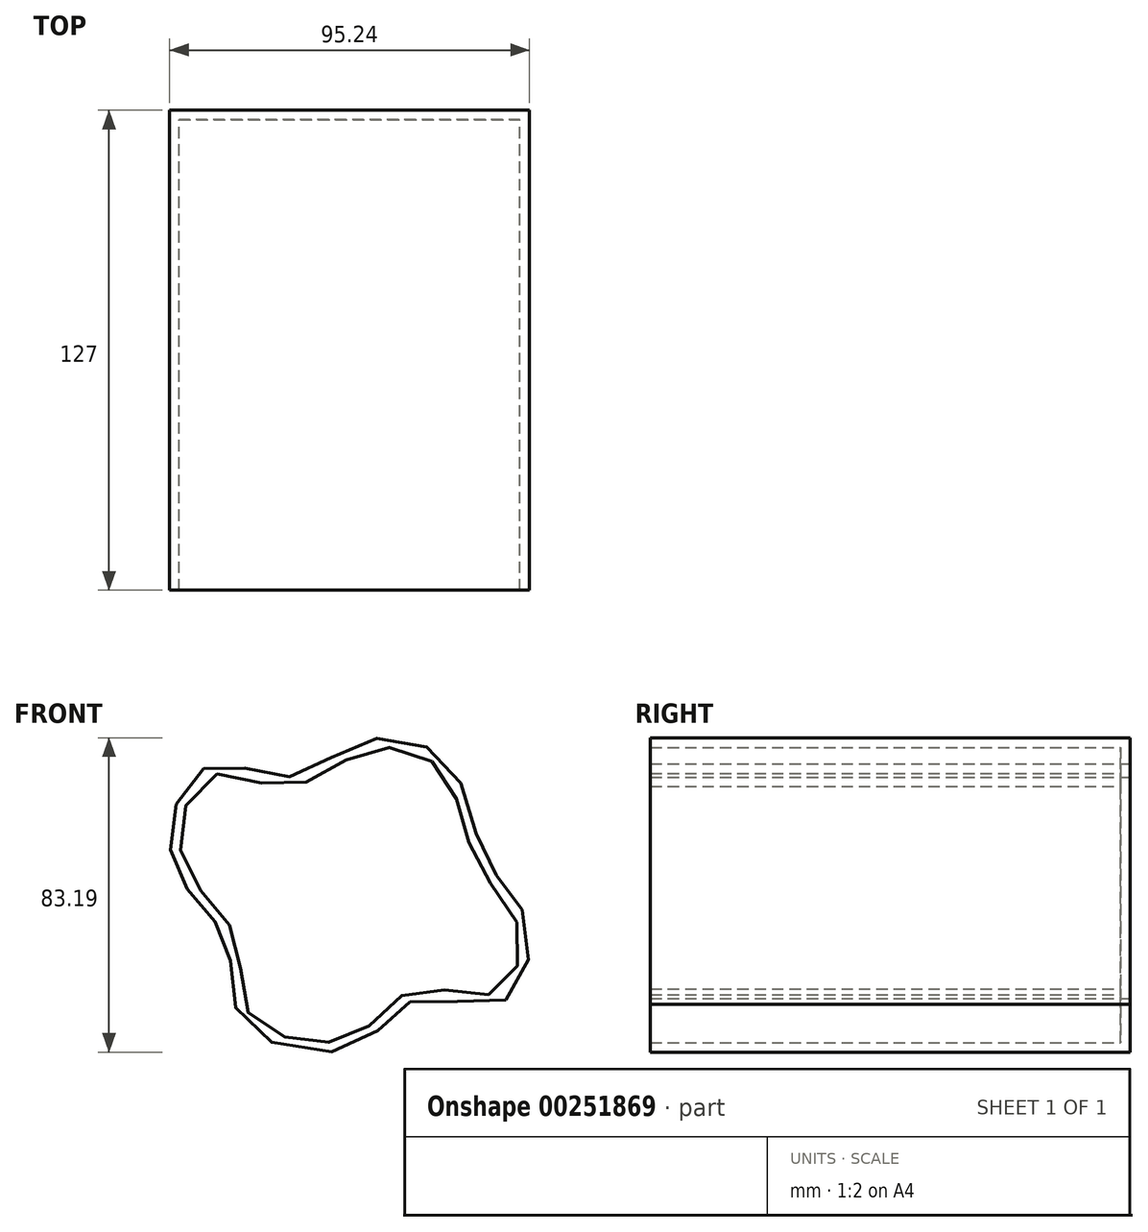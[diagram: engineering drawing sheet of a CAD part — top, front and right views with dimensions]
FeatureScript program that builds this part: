
annotation { "Feature Type Name" : "Feature", "Feature Type Description" : "" }
export const myFeature = defineFeature(function(context is Context, id is Id, definition is map)
    precondition{}
    {
        {
            var Q0;
            Q0=qCreatedBy(makeId("Front.planeOp"),FACE);
            var sketch = newSketch(context, id + "F0", { "sketchPlane" : qUnion([Q0])});
            skFitSpline(sketch, "E0", {"points": [v(-36.63, 0) * mm, v(-40.9, 17.96) * mm, v(-29.52, 32.9) * mm, v(-9.96, 29.7) * mm, v(10.67, 39.3) * mm, v(33.07, 32.54) * mm, v(42.32, 8) * mm, v(52.99, -8) * mm, v(47.65, -29.34) * mm, v(23.83, -29.34) * mm, v(8.18, -41.43) * mm, v(-21.7, -35.39) * mm, v(-25.96, -14.4) * mm, v(-36.63, 0) * mm]});
            skSolve(sketch);
        }
        {
            var Q0;
            Q0 = qSketchRegion(id + "F0", true);
            extrude(context, id + "F1", {"entities" : qUnion([Q0]), "endBound" : BoundingType.SYMMETRIC, "depth" : 127 * mm, "offsetDistance" : 25.4 * mm});
        }
        {
            var Q0;
            Q0=makeQuery(id+"F1.opExtrude","CAP_FACE",FACE,{"disambiguationData":[OSD([sQuery(id+"F0.wireOp",EDGE,"E0")])],"isStart":false});
            shell(context, id + "F2", {"entities" : qUnion([Q0]), "thickness" : 2.54 * mm});
        }
    });
